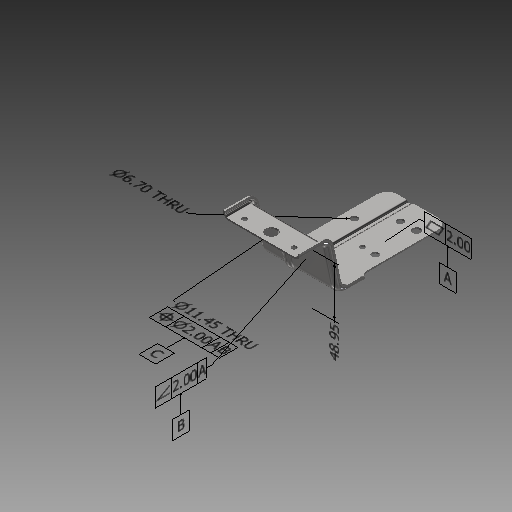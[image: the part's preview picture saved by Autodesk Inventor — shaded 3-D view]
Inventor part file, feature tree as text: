
AUTODESK INVENTOR PART (.ipt)
format: ipt  version: 2019 (Build 230136000, 136)  size: 552,448 bytes
history: native  units: mm
features: fillet x5, sketch x5, extrude x4, hole x4, projected_geometry x2, plane x1, shell x1, mirror x1
ambient origin geometry x8: Origin, YZ Plane, XZ Plane, XY Plane, X Axis, Y Axis, Z Axis, Center Point
bodies: Solid1 (feature_tree)
feature tree (23):
  extrude  "Extrusion1"  Depth=6.3mm
  fillet  "Fillet1"  Radius=26.0mm
  plane  "Work Plane1"
  extrude  "Extrusion2"  Depth=14.0mm
  fillet  "Fillet2"  Radius=5.0mm
  fillet  "Fillet3"  Radius=14.0mm
  shell  "Shell1"  Thickness=73.7mm
  extrude  "Extrusion3"  Depth=5.0mm
  extrude  "Extrusion4"  [1 undecoded]
  mirror  "Mirror1"
  fillet  "Fillet4"  Radius=2.5mm
  fillet  "Fillet5"  Radius=1.75mm
  sketch  "Sketch6"  dims[d18=9.5mm d19=2.0mm d20=3.25mm d21=1.5mm d22=4.0mm d23=0.0mm d24=18.0mm d26=7.25mm d27=9.0mm d28=7.25mm d29=77.743419mm d30=4.0mm d31=0.0mm d32=6.3mm d33=10.0mm d34=7.865mm d35=9.795mm d36=7.865mm d37=24.0mm d38=24.0mm d39=7.5mm d40=20.0mm d41=20.0mm d42=4.4mm d43=20.0mm d44=90.0mm d45=90.0mm d46=130.0mm d47=130.0mm d48=110.0mm d49=6.7mm d50=6.0mm d51=4.0mm d52=2.0mm d53=90.0deg d54=8.0mm d55=20.594885mm d56=8.0mm d57=6.0mm d58=4.0mm d59=2.0mm d60=90.0deg d61=8.0mm d62=20.594885mm d63=5.0mm d64=6.0mm d65=4.0mm d66=2.0mm d67=90.0deg d68=8.0mm d69=20.594885mm d70=11.45mm d71=6.0mm d72=4.0mm d73=2.0mm d74=90.0deg d75=8.0mm d76=20.594885mm d77=5.653131mm d78=4.900525mm d82=6.771116mm d83=3.470975mm d87=55.533837mm d88=10.0mm d89=0.0mm d94=8.447298mm d96=6.644929mm d97=6.542779mm d98=48.95mm]
  hole  "Hole1"  [1 undecoded]
  hole  "Hole2"  [1 undecoded]
  hole  "Hole3"  [1 undecoded]
  hole  "Hole4"  [1 undecoded]
  sketch  "Sketch2"  dims[d0=17.802358mm d1=6.3mm d2=26.0mm]
  sketch  "Sketch3"  dims[d3=151.25mm d4=55.25mm d5=5.0mm d6=14.0mm d7=73.7mm d8=0.0mm]
  sketch  "Sketch4"  dims[d9=5.0mm d12=16.5mm]
  sketch  "Sketch5"  dims[d13=4.0mm d14=0.0mm d15=-8.137mm d16=2.5mm d17=1.75mm]
  projected_geometry  "Project Cut Edges2"
  projected_geometry  "Project Cut Edges3"
note: 5 required parameter values undecoded (feature->parameter linkage not recoverable at this tier; creation-order binding heuristic only, values carry confidence <= 0.55)
